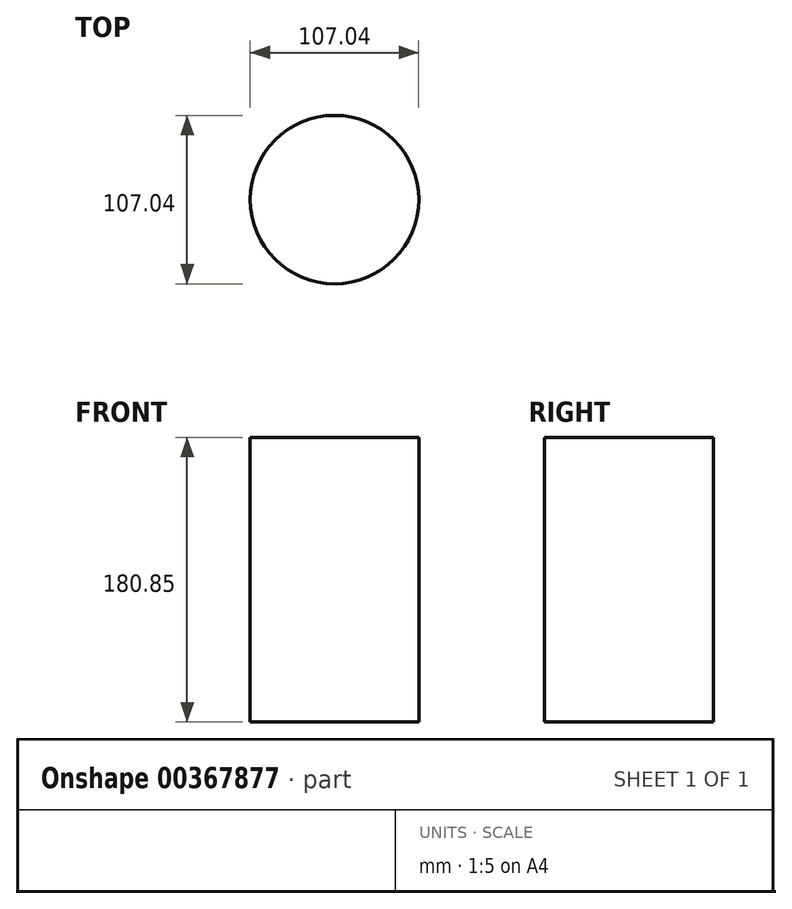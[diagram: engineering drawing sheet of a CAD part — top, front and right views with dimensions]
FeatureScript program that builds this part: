
annotation { "Feature Type Name" : "Feature", "Feature Type Description" : "" }
export const myFeature = defineFeature(function(context is Context, id is Id, definition is map)
    precondition{}
    {
        {
            var Q0;
            Q0=qCreatedBy(makeId("Top.planeOp"),FACE);
            var sketch = newSketch(context, id + "F0", { "sketchPlane" : qUnion([Q0])});
            skCircle(sketch, "E0", {"center": v(0, 0) * mm, "radius": 53.52 * mm});
            skSolve(sketch);
        }
        {
            var Q0;
            Q0=makeQuery(id+"F0.imprint","IMPRINT",FACE,{"disambiguationData":[TD([[makeQuery(id+"F0.imprint","IMPRINT",EDGE,{"derivedFrom":sQuery(id+"F0.wireOp",EDGE,"E0")}),1.0]])]});
            extrude(context, id + "F1", {"entities" : qUnion([Q0]), "depth" : 113.03 * mm});
        }
        {
            var Q0;
            Q0=makeQuery(id+"F1.opExtrude","CAP_FACE",FACE,{"disambiguationData":[OSD([sQuery(id+"F0.wireOp",EDGE,"E0")])],"isStart":false});
            extrude(context, id + "F2", {"entities" : qUnion([Q0]), "operationType" : NewBodyOperationType.ADD, "depth" : 42.42 * mm});
        }
        {
            var Q0;
            Q0=makeQuery(id+"F2.opExtrude","CAP_FACE",FACE,{"disambiguationData":[OSD([sQuery(id+"F0.wireOp",EDGE,"E0")])],"isStart":false});
            var sketch = newSketch(context, id + "F3", { "sketchPlane" : qUnion([Q0])});
            skCircle(sketch, "E1", {"center": v(0, 0) * mm, "radius": 44.6 * mm});
            skCircle(sketch, "E2", {"center": v(0, 0) * mm, "radius": 36 * mm});
            skSolve(sketch);
        }
        {
            var Q0;
            Q0=makeQuery(id+"F3.imprint","IMPRINT",FACE,{"disambiguationData":[TD([[makeQuery(id+"F3.imprint","IMPRINT",EDGE,{"derivedFrom":sQuery(id+"F3.wireOp",EDGE,"E2")}),1.0]])]});
            extrude(context, id + "F4", {"entities" : qUnion([Q0]), "operationType" : NewBodyOperationType.ADD, "depth" : 25.4 * mm});
        }
        {
            var Q0;
            Q0=makeQuery(id+"F2.opExtrude","CAP_FACE",FACE,{"disambiguationData":[OSD([sQuery(id+"F0.wireOp",EDGE,"E0")])],"isStart":false});
            extrude(context, id + "F5", {"entities" : qUnion([Q0]), "operationType" : NewBodyOperationType.ADD, "depth" : 25.4 * mm});
        }
    });
